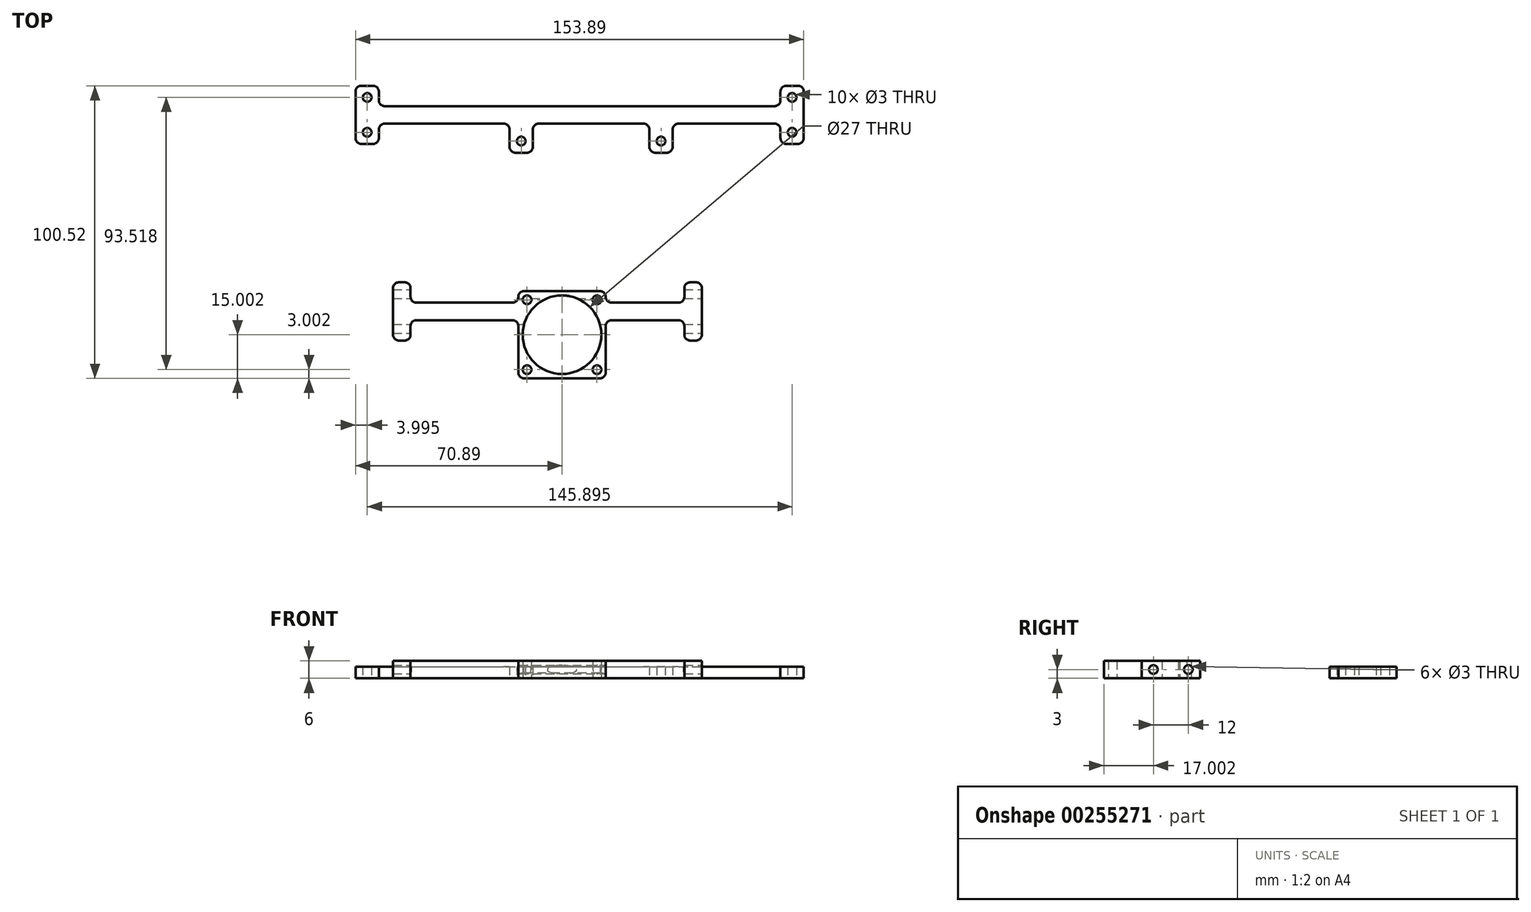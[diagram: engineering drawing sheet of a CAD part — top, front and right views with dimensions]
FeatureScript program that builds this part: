
annotation { "Feature Type Name" : "Feature", "Feature Type Description" : "" }
export const myFeature = defineFeature(function(context is Context, id is Id, definition is map)
    precondition{}
    {
        {
            var Q0;
            Q0=qCreatedBy(makeId("Top.planeOp"),FACE);
            var sketch = newSketch(context, id + "F0", { "sketchPlane" : qUnion([Q0])});
            skPoint(sketch, "E0.rect.middle", {"position": v(0, 0) * mm});
            skLineSegment(sketch, "E1.bottom", {"start": v(30, 3) * mm, "end": v(38, 3) * mm, "construction": true});
            skLineSegment(sketch, "E1.top", {"start": v(30, -7) * mm, "end": v(38, -7) * mm});
            skLineSegment(sketch, "E1.left", {"start": v(30, 3) * mm, "end": v(30, -7) * mm});
            skLineSegment(sketch, "E1.right", {"start": v(38, 3) * mm, "end": v(38, -7) * mm});
            skLineSegment(sketch, "E2.bottom", {"start": v(-10, 3) * mm, "end": v(-18, 3) * mm, "construction": true});
            skLineSegment(sketch, "E2.top", {"start": v(-10, -7) * mm, "end": v(-18, -7) * mm});
            skLineSegment(sketch, "E2.left", {"start": v(-10, 3) * mm, "end": v(-10, -7) * mm});
            skLineSegment(sketch, "E2.right", {"start": v(-18, 3) * mm, "end": v(-18, -7) * mm});
            skLineSegment(sketch, "E3", {"start": v(-14, -7) * mm, "end": v(-14, -3) * mm, "construction": true});
            skLineSegment(sketch, "E4", {"start": v(34, -7) * mm, "end": v(34, -3) * mm, "construction": true});
            skCircle(sketch, "E5", {"center": v(34, -3) * mm, "radius": 1.5 * mm});
            skCircle(sketch, "E6", {"center": v(-14, -3) * mm, "radius": 1.5 * mm});
            skLineSegment(sketch, "E7.bottom", {"start": v(75, -4) * mm, "end": v(83, -4) * mm});
            skLineSegment(sketch, "E7.top", {"start": v(75, 16) * mm, "end": v(83, 16) * mm});
            skLineSegment(sketch, "E7.left", {"start": v(75, -4) * mm, "end": v(75, 16) * mm});
            skLineSegment(sketch, "E7.right", {"start": v(83, -4) * mm, "end": v(83, 16) * mm});
            skLineSegment(sketch, "E8.bottom", {"start": v(-62.9, -4) * mm, "end": v(-70.9, -4) * mm});
            skLineSegment(sketch, "E8.top", {"start": v(-62.9, 16) * mm, "end": v(-70.9, 16) * mm});
            skLineSegment(sketch, "E8.left", {"start": v(-62.9, -4) * mm, "end": v(-62.9, 16) * mm});
            skLineSegment(sketch, "E8.right", {"start": v(-70.9, -4) * mm, "end": v(-70.9, 16) * mm});
            skLineSegment(sketch, "E9", {"start": v(-66.9, 12) * mm, "end": v(79, 12) * mm, "construction": true});
            skCircle(sketch, "E10", {"center": v(-66.9, 12) * mm, "radius": 1.5 * mm});
            skCircle(sketch, "E11", {"center": v(79, 12) * mm, "radius": 1.5 * mm});
            skLineSegment(sketch, "E12", {"start": v(-66.9, 16) * mm, "end": v(-66.9, 12) * mm, "construction": true});
            skPoint(sketch, "E13.rect.middle", {"position": v(0, -61.52) * mm});
            skLineSegment(sketch, "E14", {"start": v(79, 16) * mm, "end": v(79, 12) * mm, "construction": true});
            skLineSegment(sketch, "E15.rect.bottom", {"start": v(42, -51.52) * mm, "end": v(48, -51.52) * mm});
            skLineSegment(sketch, "E15.rect.top", {"start": v(42, -71.52) * mm, "end": v(48, -71.52) * mm});
            skLineSegment(sketch, "E15.rect.left", {"start": v(42, -51.52) * mm, "end": v(42, -71.52) * mm});
            skLineSegment(sketch, "E15.rect.right", {"start": v(48, -51.52) * mm, "end": v(48, -71.52) * mm});
            skPoint(sketch, "E15.rect.middle", {"position": v(45, -61.52) * mm});
            skLineSegment(sketch, "E16.rect.bottom", {"start": v(-58, -51.52) * mm, "end": v(-52, -51.52) * mm});
            skLineSegment(sketch, "E16.rect.top", {"start": v(-58, -71.52) * mm, "end": v(-52, -71.52) * mm});
            skLineSegment(sketch, "E16.rect.left", {"start": v(-58, -51.52) * mm, "end": v(-58, -71.52) * mm});
            skLineSegment(sketch, "E16.rect.right", {"start": v(-52, -51.52) * mm, "end": v(-52, -71.52) * mm});
            skPoint(sketch, "E16.rect.middle", {"position": v(-55, -61.52) * mm});
            skLineSegment(sketch, "E17", {"start": v(-55, -61.52) * mm, "end": v(45, -61.52) * mm, "construction": true});
            skLineSegment(sketch, "E18.rect.right", {"start": v(-15, -55.46) * mm, "end": v(-15, -69.52) * mm, "construction": true});
            skPoint(sketch, "E18.rect.middle", {"position": v(-38.83, -61.52) * mm});
            skLineSegment(sketch, "E19.rect.left", {"start": v(15, -55.46) * mm, "end": v(15, -69.52) * mm, "construction": true});
            skPoint(sketch, "E19.rect.middle", {"position": v(27.13, -61.52) * mm});
            skLineSegment(sketch, "E20", {"start": v(-66.9, -4) * mm, "end": v(-66.9, 0) * mm, "construction": true});
            skCircle(sketch, "E21", {"center": v(-66.9, 0) * mm, "radius": 1.5 * mm});
            skLineSegment(sketch, "E22", {"start": v(79, -4) * mm, "end": v(79, 0) * mm, "construction": true});
            skCircle(sketch, "E23", {"center": v(79, 0) * mm, "radius": 1.5 * mm});
            skLineSegment(sketch, "E24.bottom", {"start": v(15, -54.52) * mm, "end": v(-15, -54.52) * mm});
            skLineSegment(sketch, "E24.top", {"start": v(15, -84.52) * mm, "end": v(-15, -84.52) * mm});
            skLineSegment(sketch, "E24.left", {"start": v(15, -54.52) * mm, "end": v(15, -84.52) * mm});
            skLineSegment(sketch, "E24.right", {"start": v(-15, -54.52) * mm, "end": v(-15, -84.52) * mm});
            skLineSegment(sketch, "E25", {"start": v(0, -84.52) * mm, "end": v(0, -61.52) * mm, "construction": true});
            skLineSegment(sketch, "E26", {"start": v(0, 0) * mm, "end": v(0, -61.52) * mm, "construction": true});
            skLineSegment(sketch, "E27.0", {"start": v(9, -60.52) * mm, "end": v(-9, -60.52) * mm});
            skLineSegment(sketch, "E27.1", {"start": v(9, -60.52) * mm, "end": v(9, -78.52) * mm});
            skLineSegment(sketch, "E27.2", {"start": v(9, -78.52) * mm, "end": v(-9, -78.52) * mm});
            skLineSegment(sketch, "E27.3", {"start": v(-9, -60.52) * mm, "end": v(-9, -78.52) * mm});
            skLineSegment(sketch, "E28", {"start": v(15, -54.52) * mm, "end": v(9, -60.52) * mm, "construction": true});
            skLineSegment(sketch, "E29", {"start": v(-9, -60.52) * mm, "end": v(-15, -54.52) * mm, "construction": true});
            skLineSegment(sketch, "E30", {"start": v(9, -78.52) * mm, "end": v(15, -84.52) * mm, "construction": true});
            skLineSegment(sketch, "E31", {"start": v(-15, -84.52) * mm, "end": v(-9, -78.52) * mm, "construction": true});
            skCircle(sketch, "E32", {"center": v(12, -57.52) * mm, "radius": 1.5 * mm});
            skCircle(sketch, "E33", {"center": v(-12, -57.52) * mm, "radius": 1.5 * mm});
            skCircle(sketch, "E34", {"center": v(12, -81.52) * mm, "radius": 1.5 * mm});
            skCircle(sketch, "E35", {"center": v(-12, -81.52) * mm, "radius": 1.5 * mm});
            skLineSegment(sketch, "E36", {"start": v(-52, -58.52) * mm, "end": v(42, -58.52) * mm});
            skLineSegment(sketch, "E37.0", {"start": v(-52, -64.52) * mm, "end": v(42, -64.52) * mm});
            skLineSegment(sketch, "E38", {"start": v(-62.9, 9) * mm, "end": v(75, 9) * mm});
            skLineSegment(sketch, "E39.0", {"start": v(-62.9, 3) * mm, "end": v(75, 3) * mm});
            skLineSegment(sketch, "E40", {"start": v(-15, -69.52) * mm, "end": v(15, -69.52) * mm});
            skCircle(sketch, "E41", {"center": v(0, -69.52) * mm, "radius": 13.5 * mm});
            skSolve(sketch);
        }
        {
            var Q0;
            {var subQ3=sQuery(id+"F0.wireOp",EDGE,"E8.bottom");Q0=makeQuery(id+"F0.imprint","IMPRINT",FACE,{"disambiguationData":[TD([[makeQuery(id+"F0.imprint","IMPRINT",EDGE,{"derivedFrom":subQ3}),-1.0]])]});}
            var Q1;
            {var subQ3=sQuery(id+"F0.wireOp",EDGE,"E0.rect.bottom");Q1=makeQuery(id+"F0.imprint","IMPRINT",FACE,{"disambiguationData":[TD([[makeQuery(id+"F0.imprint","IMPRINT",EDGE,{"derivedFrom":subQ3}),1.0]])]});}
            var Q2;
            Q2=makeQuery(id+"F0.imprint","IMPRINT",FACE,{"disambiguationData":[TD([[makeQuery(id+"F0.imprint","IMPRINT",EDGE,{"derivedFrom":sQuery(id+"F0.wireOp",EDGE,"E2.top")}),-1.0]])]});
            var Q3;
            Q3=makeQuery(id+"F0.imprint","IMPRINT",FACE,{"disambiguationData":[TD([[makeQuery(id+"F0.imprint","IMPRINT",EDGE,{"derivedFrom":sQuery(id+"F0.wireOp",EDGE,"E1.top")}),1.0]])]});
            var Q4;
            {var subQ3=sQuery(id+"F0.wireOp",EDGE,"E7.bottom");Q4=makeQuery(id+"F0.imprint","IMPRINT",FACE,{"disambiguationData":[TD([[makeQuery(id+"F0.imprint","IMPRINT",EDGE,{"derivedFrom":subQ3}),1.0]])]});}
            var Q5;
            {var subQ1=sQuery(id+"F0.wireOp",EDGE,"E38");Q5=makeQuery(id+"F0.imprint","IMPRINT",FACE,{"disambiguationData":[TD([[makeQuery(id+"F0.imprint","IMPRINT",EDGE,{"derivedFrom":subQ1}),-1.0]])]});}
            var Q6;
            Q6=makeQuery(id+"F0.imprint","IMPRINT",FACE,{"disambiguationData":[TD([[makeQuery(id+"F0.imprint","IMPRINT",EDGE,{"derivedFrom":sQuery(id+"F0.wireOp",EDGE,"E2.top")}),-1.0]])]});
            var Q7;
            Q7=makeQuery(id+"F0.imprint","IMPRINT",FACE,{"disambiguationData":[TD([[makeQuery(id+"F0.imprint","IMPRINT",EDGE,{"derivedFrom":sQuery(id+"F0.wireOp",EDGE,"E1.top")}),1.0]])]});
            extrude(context, id + "F1", {"entities" : qUnion([Q0, Q1, Q2, Q3, Q4, Q5, Q6, Q7]), "depth" : 4 * mm});
        }
        {
            var Q0;
            Q0=makeQuery(id+"F1.opExtrude","SWEPT_EDGE",EDGE,{"disambiguationData":[OSD([sQuery(id+"F0.wireOp",EDGE,"E8.bottom"),sQuery(id+"F0.wireOp",EDGE,"E8.right")])]});
            var Q1;
            Q1=makeQuery(id+"F1.opExtrude","SWEPT_EDGE",EDGE,{"disambiguationData":[OSD([sQuery(id+"F0.wireOp",EDGE,"E2.top"),sQuery(id+"F0.wireOp",EDGE,"E2.right")])]});
            var Q2;
            Q2=makeQuery(id+"F1.opExtrude","SWEPT_EDGE",EDGE,{"disambiguationData":[OSD([sQuery(id+"F0.wireOp",EDGE,"E2.top"),sQuery(id+"F0.wireOp",EDGE,"E2.left")])]});
            var Q3;
            Q3=makeQuery(id+"F1.opExtrude","SWEPT_EDGE",EDGE,{"disambiguationData":[OSD([sQuery(id+"F0.wireOp",EDGE,"E8.top"),sQuery(id+"F0.wireOp",EDGE,"E8.right")])]});
            var Q4;
            Q4=makeQuery(id+"F1.opExtrude","SWEPT_EDGE",EDGE,{"disambiguationData":[OSD([sQuery(id+"F0.wireOp",EDGE,"E1.top"),sQuery(id+"F0.wireOp",EDGE,"E1.left")])]});
            var Q5;
            Q5=makeQuery(id+"F1.opExtrude","SWEPT_EDGE",EDGE,{"disambiguationData":[OSD([sQuery(id+"F0.wireOp",EDGE,"E1.top"),sQuery(id+"F0.wireOp",EDGE,"E1.right")])]});
            var Q6;
            Q6=makeQuery(id+"F1.opExtrude","SWEPT_EDGE",EDGE,{"disambiguationData":[OSD([sQuery(id+"F0.wireOp",EDGE,"E7.bottom"),sQuery(id+"F0.wireOp",EDGE,"E7.right")])]});
            var Q7;
            Q7=makeQuery(id+"F1.opExtrude","SWEPT_EDGE",EDGE,{"disambiguationData":[OSD([sQuery(id+"F0.wireOp",EDGE,"E7.top"),sQuery(id+"F0.wireOp",EDGE,"E7.right")])]});
            var Q8;
            Q8=makeQuery(id+"F1.opExtrude","SWEPT_EDGE",EDGE,{"disambiguationData":[OSD([sQuery(id+"F0.wireOp",EDGE,"E7.top"),sQuery(id+"F0.wireOp",EDGE,"E7.left")])]});
            var Q9;
            Q9=makeQuery(id+"F1.opExtrude","SWEPT_EDGE",EDGE,{"disambiguationData":[OSD([sQuery(id+"F0.wireOp",EDGE,"E8.top"),sQuery(id+"F0.wireOp",EDGE,"E8.left")])]});
            var Q10;
            Q10=makeQuery(id+"F1.opExtrude","SWEPT_EDGE",EDGE,{"disambiguationData":[OSD([sQuery(id+"F0.wireOp",EDGE,"E0.rect.bottom"),sQuery(id+"F0.wireOp",EDGE,"E8.left")])]});
            var Q11;
            Q11=makeQuery(id+"F1.opExtrude","SWEPT_EDGE",EDGE,{"disambiguationData":[OSD([sQuery(id+"F0.wireOp",EDGE,"E0.rect.bottom"),sQuery(id+"F0.wireOp",EDGE,"E7.left")])]});
            var Q12;
            Q12=makeQuery(id+"F1.opExtrude","SWEPT_EDGE",EDGE,{"disambiguationData":[OSD([sQuery(id+"F0.wireOp",EDGE,"E0.rect.top"),sQuery(id+"F0.wireOp",EDGE,"E1.left")])]});
            var Q13;
            Q13=makeQuery(id+"F1.opExtrude","SWEPT_EDGE",EDGE,{"disambiguationData":[OSD([sQuery(id+"F0.wireOp",EDGE,"E0.rect.top"),sQuery(id+"F0.wireOp",EDGE,"E2.right")])]});
            var Q14;
            Q14=makeQuery(id+"F1.opExtrude","SWEPT_EDGE",EDGE,{"disambiguationData":[OSD([sQuery(id+"F0.wireOp",EDGE,"E0.rect.top"),sQuery(id+"F0.wireOp",EDGE,"E2.left")])]});
            var Q15;
            Q15=makeQuery(id+"F1.opExtrude","SWEPT_EDGE",EDGE,{"disambiguationData":[OSD([sQuery(id+"F0.wireOp",EDGE,"E0.rect.top"),sQuery(id+"F0.wireOp",EDGE,"E1.right")])]});
            fillet(context, id + "F6", {"entities" : qUnion([Q0, Q1, Q2, Q3, Q4, Q5, Q6, Q7, Q8, Q9, Q10, Q11, Q12, Q13, Q14, Q15]), "radius" : 2 * mm, "tangentPropagation" : true, "allowEdgeOverflow" : false});
        }
        {
            var Q0;
            {var subQ4=sQuery(id+"F0.wireOp",EDGE,"E16.rect.bottom");Q0=makeQuery(id+"F0.imprint","IMPRINT",FACE,{"disambiguationData":[TD([[makeQuery(id+"F0.imprint","IMPRINT",EDGE,{"derivedFrom":subQ4}),-1.0]])]});}
            var Q1;
            {var subQ0=sQuery(id+"F0.wireOp",EDGE,"E18.rect.bottom");Q1=makeQuery(id+"F0.imprint","IMPRINT",FACE,{"disambiguationData":[TD([[makeQuery(id+"F0.imprint","IMPRINT",EDGE,{"derivedFrom":subQ0}),-1.0]])]});}
            var Q2;
            Q2=makeQuery(id+"F0.imprint","IMPRINT",FACE,{"disambiguationData":[TD([[makeQuery(id+"F0.imprint","IMPRINT",EDGE,{"derivedFrom":sQuery(id+"F0.wireOp",EDGE,"E13.rect.bottom")}),-1.0]])]});
            var Q3;
            {var subQ4=sQuery(id+"F0.wireOp",EDGE,"E15.rect.bottom");Q3=makeQuery(id+"F0.imprint","IMPRINT",FACE,{"disambiguationData":[TD([[makeQuery(id+"F0.imprint","IMPRINT",EDGE,{"derivedFrom":subQ4}),-1.0]])]});}
            var Q4;
            {var subQ1=sQuery(id+"F0.wireOp",EDGE,"E19.rect.bottom");Q4=makeQuery(id+"F0.imprint","IMPRINT",FACE,{"disambiguationData":[TD([[makeQuery(id+"F0.imprint","IMPRINT",EDGE,{"derivedFrom":subQ1}),-1.0]])]});}
            var Q5;
            {var subQ3=sQuery(id+"F0.wireOp",EDGE,"E24.bottom");Q5=makeQuery(id+"F0.imprint","IMPRINT",FACE,{"disambiguationData":[TD([[makeQuery(id+"F0.imprint","IMPRINT",EDGE,{"derivedFrom":subQ3}),1.0]])]});}
            var Q6;
            {var subQ3=sQuery(id+"F0.wireOp",EDGE,"E16.rect.right");var subQ5=sQuery(id+"F0.wireOp",EDGE,"E36");var subQ7=makeQuery(id+"F0.imprint","INTERSECT",VERTEX,{"derivedFrom":[subQ3,subQ5]});Q6=makeQuery(id+"F0.imprint","IMPRINT",FACE,{"disambiguationData":[TD([[makeQuery(id+"F0.imprint","IMPRINT",EDGE,{"disambiguationData":[TD([[subQ7,-1.0]])],"derivedFrom":subQ3}),1.0]])]});}
            var Q7;
            {var subQ10=sQuery(id+"F0.wireOp",EDGE,"E24.top");Q7=makeQuery(id+"F0.imprint","IMPRINT",FACE,{"disambiguationData":[TD([[makeQuery(id+"F0.imprint","IMPRINT",EDGE,{"derivedFrom":subQ10}),-1.0]])]});}
            var Q8;
            {var subQ3=sQuery(id+"F0.wireOp",EDGE,"E24.right");var subQ5=sQuery(id+"F0.wireOp",EDGE,"E36");var subQ7=makeQuery(id+"F0.imprint","INTERSECT",VERTEX,{"derivedFrom":[subQ3,subQ5]});Q8=makeQuery(id+"F0.imprint","IMPRINT",FACE,{"disambiguationData":[TD([[makeQuery(id+"F0.imprint","IMPRINT",EDGE,{"disambiguationData":[TD([[subQ7,-1.0]])],"derivedFrom":subQ3}),1.0]])]});}
            var Q9;
            {var subQ3=sQuery(id+"F0.wireOp",EDGE,"E24.left");var subQ5=sQuery(id+"F0.wireOp",EDGE,"E36");var subQ7=makeQuery(id+"F0.imprint","INTERSECT",VERTEX,{"derivedFrom":[subQ3,subQ5]});Q9=makeQuery(id+"F0.imprint","IMPRINT",FACE,{"disambiguationData":[TD([[makeQuery(id+"F0.imprint","IMPRINT",EDGE,{"disambiguationData":[TD([[subQ7,-1.0]])],"derivedFrom":subQ3}),-1.0]])]});}
            var Q10;
            {var subQ3=sQuery(id+"F0.wireOp",EDGE,"E15.rect.left");var subQ5=sQuery(id+"F0.wireOp",EDGE,"E36");var subQ7=makeQuery(id+"F0.imprint","INTERSECT",VERTEX,{"derivedFrom":[subQ3,subQ5]});Q10=makeQuery(id+"F0.imprint","IMPRINT",FACE,{"disambiguationData":[TD([[makeQuery(id+"F0.imprint","IMPRINT",EDGE,{"disambiguationData":[TD([[subQ7,-1.0]])],"derivedFrom":subQ3}),-1.0]])]});}
            var Q11;
            {var subQ1=sQuery(id+"F0.wireOp",EDGE,"E40");var subQ5=sQuery(id+"F0.wireOp",EDGE,"E24.right");var subQ6=makeQuery(id+"F0.imprint","INTERSECT",VERTEX,{"derivedFrom":[subQ5,subQ1]});Q11=makeQuery(id+"F0.imprint","IMPRINT",FACE,{"disambiguationData":[TD([[makeQuery(id+"F0.imprint","IMPRINT",EDGE,{"disambiguationData":[TD([[subQ6,1.0]])],"derivedFrom":subQ5}),1.0]])]});}
            var Q12;
            {var subQ1=sQuery(id+"F0.wireOp",EDGE,"E40");var subQ5=sQuery(id+"F0.wireOp",EDGE,"E24.left");var subQ6=makeQuery(id+"F0.imprint","INTERSECT",VERTEX,{"derivedFrom":[subQ5,subQ1]});Q12=makeQuery(id+"F0.imprint","IMPRINT",FACE,{"disambiguationData":[TD([[makeQuery(id+"F0.imprint","IMPRINT",EDGE,{"disambiguationData":[TD([[subQ6,1.0]])],"derivedFrom":subQ5}),-1.0]])]});}
            extrude(context, id + "F2", {"entities" : qUnion([Q0, Q1, Q2, Q3, Q4, Q5, Q6, Q7, Q8, Q9, Q10, Q11, Q12]), "depth" : 6 * mm});
        }
        {
            var Q0;
            Q0=makeQuery(id+"F2.opExtrude","SWEPT_EDGE",EDGE,{"disambiguationData":[OSD([sQuery(id+"F0.wireOp",EDGE,"E13.rect.top"),sQuery(id+"F0.wireOp",EDGE,"E13.rect.left")])]});
            var Q1;
            Q1=makeQuery(id+"F2.opExtrude","SWEPT_EDGE",EDGE,{"disambiguationData":[OSD([sQuery(id+"F0.wireOp",EDGE,"E16.rect.right"),sQuery(id+"F0.wireOp",EDGE,"E18.rect.top")])]});
            var Q2;
            Q2=makeQuery(id+"F2.opExtrude","SWEPT_EDGE",EDGE,{"disambiguationData":[OSD([sQuery(id+"F0.wireOp",EDGE,"E16.rect.top"),sQuery(id+"F0.wireOp",EDGE,"E16.rect.right")])]});
            var Q3;
            Q3=makeQuery(id+"F2.opExtrude","SWEPT_EDGE",EDGE,{"disambiguationData":[OSD([sQuery(id+"F0.wireOp",EDGE,"E16.rect.top"),sQuery(id+"F0.wireOp",EDGE,"E16.rect.left")])]});
            var Q4;
            Q4=makeQuery(id+"F2.opExtrude","SWEPT_EDGE",EDGE,{"disambiguationData":[OSD([sQuery(id+"F0.wireOp",EDGE,"d886061f-8fd1-4490-8635-c47852207572.1"),sQuery(id+"F0.wireOp",EDGE,"d886061f-8fd1-4490-8635-c47852207572.2")])]});
            var Q5;
            Q5=makeQuery(id+"F2.opExtrude","SWEPT_EDGE",EDGE,{"disambiguationData":[OSD([sQuery(id+"F0.wireOp",EDGE,"d886061f-8fd1-4490-8635-c47852207572.2"),sQuery(id+"F0.wireOp",EDGE,"d886061f-8fd1-4490-8635-c47852207572.3")])]});
            var Q6;
            Q6=makeQuery(id+"F2.opExtrude","SWEPT_EDGE",EDGE,{"disambiguationData":[OSD([sQuery(id+"F0.wireOp",EDGE,"d886061f-8fd1-4490-8635-c47852207572.3"),sQuery(id+"F0.wireOp",EDGE,"E19.rect.top")])]});
            var Q7;
            Q7=makeQuery(id+"F2.opExtrude","SWEPT_EDGE",EDGE,{"disambiguationData":[OSD([sQuery(id+"F0.wireOp",EDGE,"E15.rect.top"),sQuery(id+"F0.wireOp",EDGE,"E15.rect.left")])]});
            var Q8;
            Q8=makeQuery(id+"F2.opExtrude","SWEPT_EDGE",EDGE,{"disambiguationData":[OSD([sQuery(id+"F0.wireOp",EDGE,"E15.rect.top"),sQuery(id+"F0.wireOp",EDGE,"E15.rect.right")])]});
            var Q9;
            Q9=makeQuery(id+"F2.opExtrude","SWEPT_EDGE",EDGE,{"disambiguationData":[OSD([sQuery(id+"F0.wireOp",EDGE,"E15.rect.bottom"),sQuery(id+"F0.wireOp",EDGE,"E15.rect.right")])]});
            var Q10;
            Q10=makeQuery(id+"F2.opExtrude","SWEPT_EDGE",EDGE,{"disambiguationData":[OSD([sQuery(id+"F0.wireOp",EDGE,"d886061f-8fd1-4490-8635-c47852207572.0"),sQuery(id+"F0.wireOp",EDGE,"d886061f-8fd1-4490-8635-c47852207572.3")])]});
            var Q11;
            Q11=makeQuery(id+"F2.opExtrude","SWEPT_EDGE",EDGE,{"disambiguationData":[OSD([sQuery(id+"F0.wireOp",EDGE,"E16.rect.bottom"),sQuery(id+"F0.wireOp",EDGE,"E16.rect.right")])]});
            var Q12;
            Q12=makeQuery(id+"F2.opExtrude","SWEPT_EDGE",EDGE,{"disambiguationData":[OSD([sQuery(id+"F0.wireOp",EDGE,"d886061f-8fd1-4490-8635-c47852207572.1"),sQuery(id+"F0.wireOp",EDGE,"E18.rect.top")])]});
            var Q13;
            Q13=makeQuery(id+"F2.opExtrude","SWEPT_EDGE",EDGE,{"disambiguationData":[OSD([sQuery(id+"F0.wireOp",EDGE,"d886061f-8fd1-4490-8635-c47852207572.0"),sQuery(id+"F0.wireOp",EDGE,"d886061f-8fd1-4490-8635-c47852207572.1")])]});
            var Q14;
            Q14=makeQuery(id+"F2.opExtrude","SWEPT_EDGE",EDGE,{"disambiguationData":[OSD([sQuery(id+"F0.wireOp",EDGE,"E16.rect.bottom"),sQuery(id+"F0.wireOp",EDGE,"E16.rect.left")])]});
            var Q15;
            Q15=makeQuery(id+"F2.opExtrude","SWEPT_EDGE",EDGE,{"disambiguationData":[OSD([sQuery(id+"F0.wireOp",EDGE,"E15.rect.left"),sQuery(id+"F0.wireOp",EDGE,"E19.rect.top")])]});
            var Q16;
            Q16=makeQuery(id+"F2.opExtrude","SWEPT_EDGE",EDGE,{"disambiguationData":[OSD([sQuery(id+"F0.wireOp",EDGE,"E15.rect.bottom"),sQuery(id+"F0.wireOp",EDGE,"E15.rect.left")])]});
            var Q17;
            Q17=makeQuery(id+"F2.opExtrude","SWEPT_EDGE",EDGE,{"disambiguationData":[OSD([sQuery(id+"F0.wireOp",EDGE,"E13.rect.top"),sQuery(id+"F0.wireOp",EDGE,"E13.rect.right")])]});
            var Q18;
            Q18=makeQuery(id+"F2.opExtrude","SWEPT_EDGE",EDGE,{"disambiguationData":[OSD([sQuery(id+"F0.wireOp",EDGE,"E13.rect.bottom"),sQuery(id+"F0.wireOp",EDGE,"E13.rect.left")])]});
            var Q19;
            Q19=makeQuery(id+"F2.opExtrude","SWEPT_EDGE",EDGE,{"disambiguationData":[OSD([sQuery(id+"F0.wireOp",EDGE,"d886061f-8fd1-4490-8635-c47852207572.3"),sQuery(id+"F0.wireOp",EDGE,"E19.rect.bottom")])]});
            var Q20;
            Q20=makeQuery(id+"F2.opExtrude","SWEPT_EDGE",EDGE,{"disambiguationData":[OSD([sQuery(id+"F0.wireOp",EDGE,"E15.rect.left"),sQuery(id+"F0.wireOp",EDGE,"E19.rect.bottom")])]});
            var Q21;
            Q21=makeQuery(id+"F2.opExtrude","SWEPT_EDGE",EDGE,{"disambiguationData":[OSD([sQuery(id+"F0.wireOp",EDGE,"E16.rect.right"),sQuery(id+"F0.wireOp",EDGE,"E18.rect.bottom")])]});
            var Q22;
            Q22=makeQuery(id+"F2.opExtrude","SWEPT_EDGE",EDGE,{"disambiguationData":[OSD([sQuery(id+"F0.wireOp",EDGE,"d886061f-8fd1-4490-8635-c47852207572.1"),sQuery(id+"F0.wireOp",EDGE,"E18.rect.bottom")])]});
            var Q23;
            Q23=makeQuery(id+"F2.opExtrude","SWEPT_EDGE",EDGE,{"disambiguationData":[OSD([sQuery(id+"F0.wireOp",EDGE,"E13.rect.bottom"),sQuery(id+"F0.wireOp",EDGE,"E13.rect.right")])]});
            var Q24;
            Q24=makeQuery(id+"F2.opExtrude","SWEPT_EDGE",EDGE,{"disambiguationData":[OSD([sQuery(id+"F0.wireOp",EDGE,"E24.bottom"),sQuery(id+"F0.wireOp",EDGE,"E24.right")])]});
            var Q25;
            Q25=makeQuery(id+"F2.opExtrude","SWEPT_EDGE",EDGE,{"disambiguationData":[OSD([sQuery(id+"F0.wireOp",EDGE,"E24.bottom"),sQuery(id+"F0.wireOp",EDGE,"E24.left")])]});
            var Q26;
            Q26=makeQuery(id+"F2.opExtrude","SWEPT_EDGE",EDGE,{"disambiguationData":[OSD([sQuery(id+"F0.wireOp",EDGE,"E24.top"),sQuery(id+"F0.wireOp",EDGE,"E24.right")])]});
            var Q27;
            Q27=makeQuery(id+"F2.opExtrude","SWEPT_EDGE",EDGE,{"disambiguationData":[OSD([sQuery(id+"F0.wireOp",EDGE,"E24.top"),sQuery(id+"F0.wireOp",EDGE,"E24.left")])]});
            var Q28;
            Q28=makeQuery(id+"F2.opExtrude","SWEPT_EDGE",EDGE,{"disambiguationData":[OSD([sQuery(id+"F0.wireOp",EDGE,"E27.0"),sQuery(id+"F0.wireOp",EDGE,"E27.1")])]});
            var Q29;
            Q29=makeQuery(id+"F2.opExtrude","SWEPT_EDGE",EDGE,{"disambiguationData":[OSD([sQuery(id+"F0.wireOp",EDGE,"E27.0"),sQuery(id+"F0.wireOp",EDGE,"E27.3")])]});
            var Q30;
            Q30=makeQuery(id+"F2.opExtrude","SWEPT_EDGE",EDGE,{"disambiguationData":[OSD([sQuery(id+"F0.wireOp",EDGE,"E27.1"),sQuery(id+"F0.wireOp",EDGE,"E27.2")])]});
            var Q31;
            Q31=makeQuery(id+"F2.opExtrude","SWEPT_FACE",FACE,{"disambiguationData":[OSD([sQuery(id+"F0.wireOp",EDGE,"E27.2")])]});
            var Q32;
            Q32=makeQuery(id+"F2.opExtrude","SWEPT_EDGE",EDGE,{"disambiguationData":[OSD([sQuery(id+"F0.wireOp",EDGE,"E24.left"),sQuery(id+"F0.wireOp",EDGE,"E36")])]});
            var Q33;
            Q33=makeQuery(id+"F2.opExtrude","SWEPT_EDGE",EDGE,{"disambiguationData":[OSD([sQuery(id+"F0.wireOp",EDGE,"E24.left"),sQuery(id+"F0.wireOp",EDGE,"E37.0")])]});
            var Q34;
            Q34=makeQuery(id+"F2.opExtrude","SWEPT_EDGE",EDGE,{"disambiguationData":[OSD([sQuery(id+"F0.wireOp",EDGE,"E24.right"),sQuery(id+"F0.wireOp",EDGE,"E37.0")])]});
            var Q35;
            Q35=makeQuery(id+"F2.opExtrude","SWEPT_EDGE",EDGE,{"disambiguationData":[OSD([sQuery(id+"F0.wireOp",EDGE,"E24.right"),sQuery(id+"F0.wireOp",EDGE,"E36")])]});
            fillet(context, id + "F3", {"entities" : qUnion([Q0, Q1, Q2, Q3, Q4, Q5, Q6, Q7, Q8, Q9, Q10, Q11, Q12, Q13, Q14, Q15, Q16, Q17, Q18, Q19, Q20, Q21, Q22, Q23, Q24, Q25, Q26, Q27, Q28, Q29, Q30, Q31, Q32, Q33, Q34, Q35]), "radius" : 2 * mm, "tangentPropagation" : true, "allowEdgeOverflow" : false});
        }
        {
            var Q0;
            Q0=makeQuery(id+"F2.opExtrude","SWEPT_FACE",FACE,{"disambiguationData":[OSD([sQuery(id+"F0.wireOp",EDGE,"E15.rect.right")])]});
            var sketch = newSketch(context, id + "F4", { "sketchPlane" : qUnion([Q0])});
            skLineSegment(sketch, "E42", {"start": v(-53.52, 3) * mm, "end": v(-69.52, 3) * mm, "construction": true});
            skCircle(sketch, "E43", {"center": v(-55.52, 3) * mm, "radius": 1.5 * mm});
            skCircle(sketch, "E44", {"center": v(-67.52, 3) * mm, "radius": 1.5 * mm});
            skSolve(sketch);
        }
        {
            var Q0;
            {var subQ0=sQuery(id+"F0.wireOp",EDGE,"E15.rect.right");var subQ1=makeQuery(id+"F3.opFillet","BLEND_EDGE",EDGE,{"blendedFrom":[makeQuery(id+"F2.opExtrude","SWEPT_EDGE",EDGE,{"disambiguationData":[OSD([sQuery(id+"F0.wireOp",EDGE,"E15.rect.bottom"),subQ0])]}),makeQuery(id+"F2.opExtrude","SWEPT_FACE",FACE,{"disambiguationData":[OSD([subQ0])]})],"blendedInto":[makeQuery(id+"F2.opExtrude","SWEPT_FACE",FACE,{"disambiguationData":[OSD([subQ0])]})]});var subQ2=sQuery(id+"F4.wireOp",EDGE,"E43");var subQ4=makeQuery(id+"F4.imprint","INTERSECT",VERTEX,{"disambiguationData":[OD(0.0)],"derivedFrom":[subQ1,subQ2]});Q0=makeQuery(id+"F4.imprint","IMPRINT",FACE,{"disambiguationData":[TD([[makeQuery(id+"F4.imprint","IMPRINT",EDGE,{"disambiguationData":[TD([[subQ4,1.0]])],"derivedFrom":subQ2}),1.0]])]});}
            var Q1;
            {var subQ0=sQuery(id+"F0.wireOp",EDGE,"E15.rect.right");var subQ1=makeQuery(id+"F3.opFillet","BLEND_EDGE",EDGE,{"blendedFrom":[makeQuery(id+"F2.opExtrude","SWEPT_EDGE",EDGE,{"disambiguationData":[OSD([sQuery(id+"F0.wireOp",EDGE,"E15.rect.bottom"),subQ0])]}),makeQuery(id+"F2.opExtrude","SWEPT_FACE",FACE,{"disambiguationData":[OSD([subQ0])]})],"blendedInto":[makeQuery(id+"F2.opExtrude","SWEPT_FACE",FACE,{"disambiguationData":[OSD([subQ0])]})]});var subQ2=sQuery(id+"F4.wireOp",EDGE,"E43");var subQ4=makeQuery(id+"F4.imprint","INTERSECT",VERTEX,{"disambiguationData":[OD(0.0)],"derivedFrom":[subQ1,subQ2]});Q1=makeQuery(id+"F4.imprint","IMPRINT",FACE,{"disambiguationData":[TD([[makeQuery(id+"F4.imprint","IMPRINT",EDGE,{"disambiguationData":[TD([[subQ4,-1.0]])],"derivedFrom":subQ2}),1.0]])]});}
            var Q2;
            {var subQ0=sQuery(id+"F0.wireOp",EDGE,"E15.rect.right");var subQ1=makeQuery(id+"F3.opFillet","BLEND_EDGE",EDGE,{"blendedFrom":[makeQuery(id+"F2.opExtrude","SWEPT_EDGE",EDGE,{"disambiguationData":[OSD([sQuery(id+"F0.wireOp",EDGE,"E15.rect.top"),subQ0])]}),makeQuery(id+"F2.opExtrude","SWEPT_FACE",FACE,{"disambiguationData":[OSD([subQ0])]})],"blendedInto":[makeQuery(id+"F2.opExtrude","SWEPT_FACE",FACE,{"disambiguationData":[OSD([subQ0])]})]});var subQ2=sQuery(id+"F4.wireOp",EDGE,"E44");var subQ4=makeQuery(id+"F4.imprint","INTERSECT",VERTEX,{"disambiguationData":[OD(0.0)],"derivedFrom":[subQ1,subQ2]});Q2=makeQuery(id+"F4.imprint","IMPRINT",FACE,{"disambiguationData":[TD([[makeQuery(id+"F4.imprint","IMPRINT",EDGE,{"disambiguationData":[TD([[subQ4,-1.0]])],"derivedFrom":subQ2}),1.0]])]});}
            var Q3;
            {var subQ0=sQuery(id+"F0.wireOp",EDGE,"E15.rect.right");var subQ1=makeQuery(id+"F3.opFillet","BLEND_EDGE",EDGE,{"blendedFrom":[makeQuery(id+"F2.opExtrude","SWEPT_EDGE",EDGE,{"disambiguationData":[OSD([sQuery(id+"F0.wireOp",EDGE,"E15.rect.top"),subQ0])]}),makeQuery(id+"F2.opExtrude","SWEPT_FACE",FACE,{"disambiguationData":[OSD([subQ0])]})],"blendedInto":[makeQuery(id+"F2.opExtrude","SWEPT_FACE",FACE,{"disambiguationData":[OSD([subQ0])]})]});var subQ2=sQuery(id+"F4.wireOp",EDGE,"E44");var subQ4=makeQuery(id+"F4.imprint","INTERSECT",VERTEX,{"disambiguationData":[OD(0.0)],"derivedFrom":[subQ1,subQ2]});Q3=makeQuery(id+"F4.imprint","IMPRINT",FACE,{"disambiguationData":[TD([[makeQuery(id+"F4.imprint","IMPRINT",EDGE,{"disambiguationData":[TD([[subQ4,1.0]])],"derivedFrom":subQ2}),1.0]])]});}
            extrude(context, id + "F5", {"entities" : qUnion([Q0, Q1, Q2, Q3]), "operationType" : NewBodyOperationType.REMOVE, "endBound" : BoundingType.THROUGH_ALL, "oppositeDirection" : true, "depth" : 25 * mm});
        }
    });
